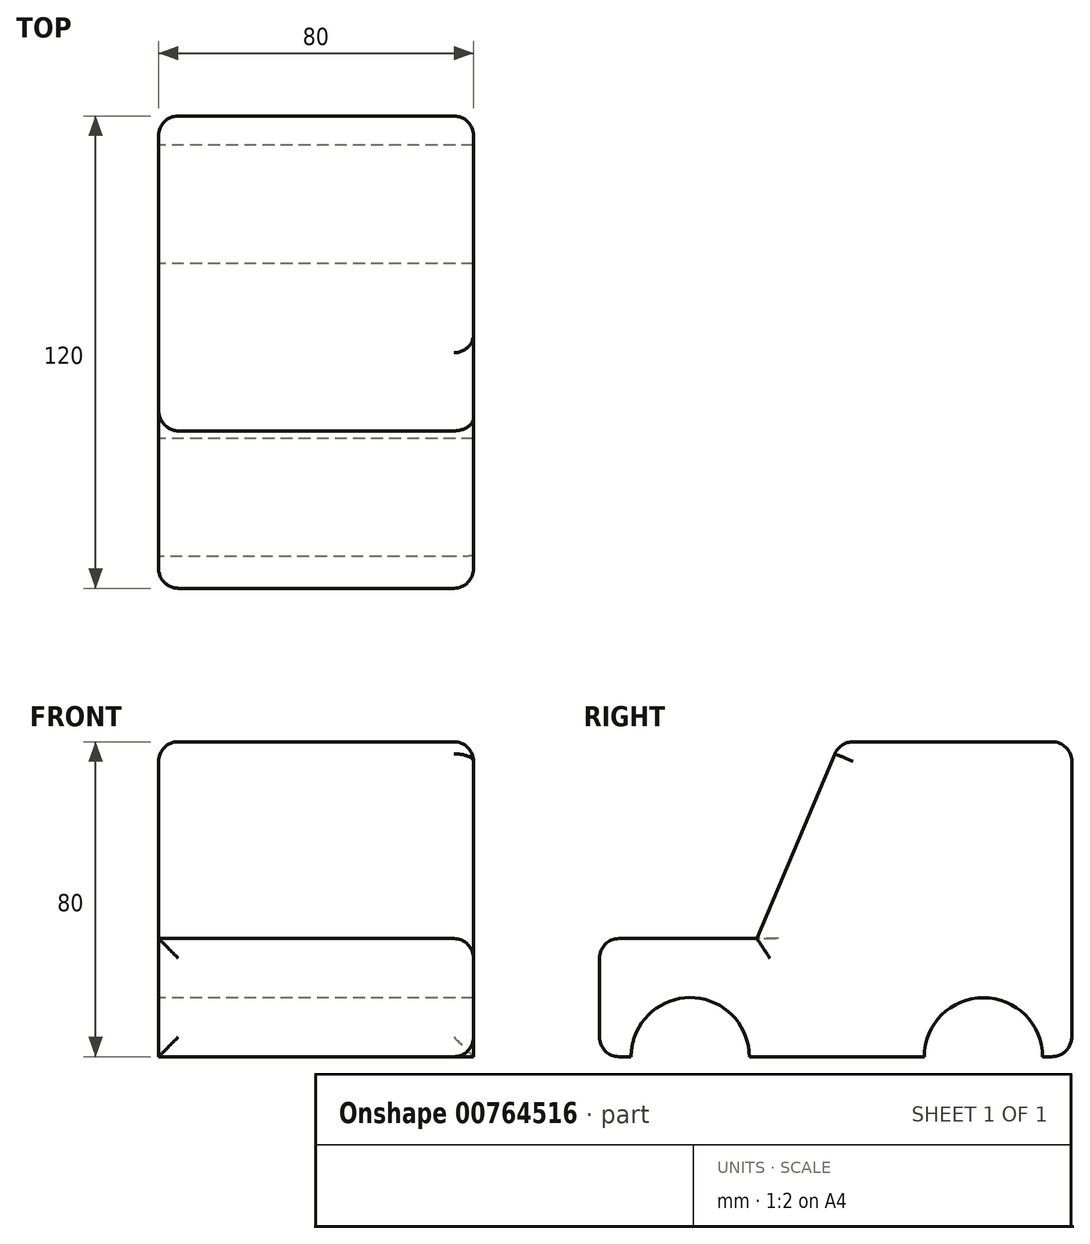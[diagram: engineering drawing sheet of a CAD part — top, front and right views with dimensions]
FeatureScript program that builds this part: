
annotation { "Feature Type Name" : "Feature", "Feature Type Description" : "" }
export const myFeature = defineFeature(function(context is Context, id is Id, definition is map)
    precondition{}
    {
        {
            var Q0;
            Q0=qCreatedBy(makeId("Right.planeOp"),FACE);
            var sketch = newSketch(context, id + "F0", { "sketchPlane" : qUnion([Q0])});
            skLineSegment(sketch, "E0", {"start": v(-63.75, 0) * mm, "end": v(-55.7, 0) * mm});
            skLineSegment(sketch, "E1", {"start": v(-63.75, 0) * mm, "end": v(-63.75, 30) * mm});
            skLineSegment(sketch, "E2", {"start": v(-63.75, 30) * mm, "end": v(-23.75, 30) * mm});
            skLineSegment(sketch, "E3", {"start": v(-23.75, 30) * mm, "end": v(-2.61, 80) * mm});
            skLineSegment(sketch, "E4", {"start": v(-2.61, 80) * mm, "end": v(56.25, 80) * mm});
            skLineSegment(sketch, "E5", {"start": v(56.25, 80) * mm, "end": v(56.25, 0) * mm});
            skArc(sketch, "E6", {"start": v(-25.7, 0) * mm, "mid": v(-40.7, 15) * mm, "end": v(-55.7, 0) * mm});
            skLineSegment(sketch, "E7.trimOffspring", {"start": v(-25.7, 0) * mm, "end": v(18.8, 0) * mm});
            skArc(sketch, "E8", {"start": v(48.8, 0) * mm, "mid": v(33.8, 15) * mm, "end": v(18.8, 0) * mm});
            skLineSegment(sketch, "E9.trimOffspring", {"start": v(48.8, 0) * mm, "end": v(56.25, 0) * mm});
            skSolve(sketch);
        }
        {
            var Q0;
            Q0 = qSketchRegion(id + "F0", true);
            extrude(context, id + "F1", {"entities" : qUnion([Q0]), "endBound" : BoundingType.SYMMETRIC, "depth" : 80 * mm, "offsetDistance" : 25 * mm});
        }
        {
            var Q0;
            Q0=makeQuery(id+"F1.opExtrude","SWEPT_EDGE",EDGE,{"disambiguationData":[OSD([sQuery(id+"F0.wireOp",EDGE,"E4"),sQuery(id+"F0.wireOp",EDGE,"E5")])]});
            var Q1;
            Q1=makeQuery(id+"F1.opExtrude","CAP_EDGE",EDGE,{"disambiguationData":[OSD([sQuery(id+"F0.wireOp",EDGE,"E5")])],"isStart":false});
            var Q2;
            Q2=makeQuery(id+"F1.opExtrude","CAP_EDGE",EDGE,{"disambiguationData":[OSD([sQuery(id+"F0.wireOp",EDGE,"E5")])],"isStart":true});
            var Q3;
            Q3=makeQuery(id+"F1.opExtrude","SWEPT_FACE",FACE,{"disambiguationData":[OSD([sQuery(id+"F0.wireOp",EDGE,"E5")])]});
            var Q4;
            Q4=makeQuery(id+"F1.opExtrude","CAP_EDGE",EDGE,{"disambiguationData":[OSD([sQuery(id+"F0.wireOp",EDGE,"E4")])],"isStart":false});
            var Q5;
            Q5=makeQuery(id+"F1.opExtrude","CAP_EDGE",EDGE,{"disambiguationData":[OSD([sQuery(id+"F0.wireOp",EDGE,"E3")])],"isStart":false});
            var Q6;
            Q6=makeQuery(id+"F1.opExtrude","CAP_EDGE",EDGE,{"disambiguationData":[OSD([sQuery(id+"F0.wireOp",EDGE,"E2")])],"isStart":false});
            var Q7;
            Q7=makeQuery(id+"F1.opExtrude","CAP_EDGE",EDGE,{"disambiguationData":[OSD([sQuery(id+"F0.wireOp",EDGE,"E1")])],"isStart":false});
            fillet(context, id + "F2", {"entities" : qUnion([Q0, Q1, Q2, Q3, Q4, Q5, Q6, Q7]), "radius" : 5 * mm, "tangentPropagation" : true, "allowEdgeOverflow" : false});
        }
        {
            var Q0;
            Q0=makeQuery(id+"F1.opExtrude","SWEPT_EDGE",EDGE,{"disambiguationData":[OSD([sQuery(id+"F0.wireOp",EDGE,"E3"),sQuery(id+"F0.wireOp",EDGE,"E4")])]});
            fillet(context, id + "F3", {"entities" : qUnion([Q0]), "radius" : 5 * mm, "tangentPropagation" : true, "allowEdgeOverflow" : false});
        }
        {
            var Q0;
            {var subQ0=sQuery(id+"F0.wireOp",EDGE,"E3");Q0=makeQuery(id+"F3.opFillet","BLEND_EDGE",EDGE,{"blendedFrom":[makeQuery(id+"F1.opExtrude","SWEPT_EDGE",EDGE,{"disambiguationData":[OSD([subQ0,sQuery(id+"F0.wireOp",EDGE,"E4")])]}),makeQuery(id+"F1.opExtrude","SWEPT_FACE",FACE,{"disambiguationData":[OSD([subQ0])]})],"blendedInto":[makeQuery(id+"F1.opExtrude","SWEPT_FACE",FACE,{"disambiguationData":[OSD([subQ0])]})]});}
            var Q1;
            Q1=makeQuery(id+"F1.opExtrude","CAP_EDGE",EDGE,{"disambiguationData":[OSD([sQuery(id+"F0.wireOp",EDGE,"E3")])],"isStart":true});
            var Q2;
            Q2=makeQuery(id+"F1.opExtrude","SWEPT_EDGE",EDGE,{"disambiguationData":[OSD([sQuery(id+"F0.wireOp",EDGE,"E1"),sQuery(id+"F0.wireOp",EDGE,"E2")])]});
            var Q3;
            Q3=makeQuery(id+"F1.opExtrude","SWEPT_FACE",FACE,{"disambiguationData":[OSD([sQuery(id+"F0.wireOp",EDGE,"E1")])]});
            fillet(context, id + "F4", {"entities" : qUnion([Q0, Q1, Q2, Q3]), "radius" : 5 * mm, "tangentPropagation" : true, "allowEdgeOverflow" : false});
        }
    });
